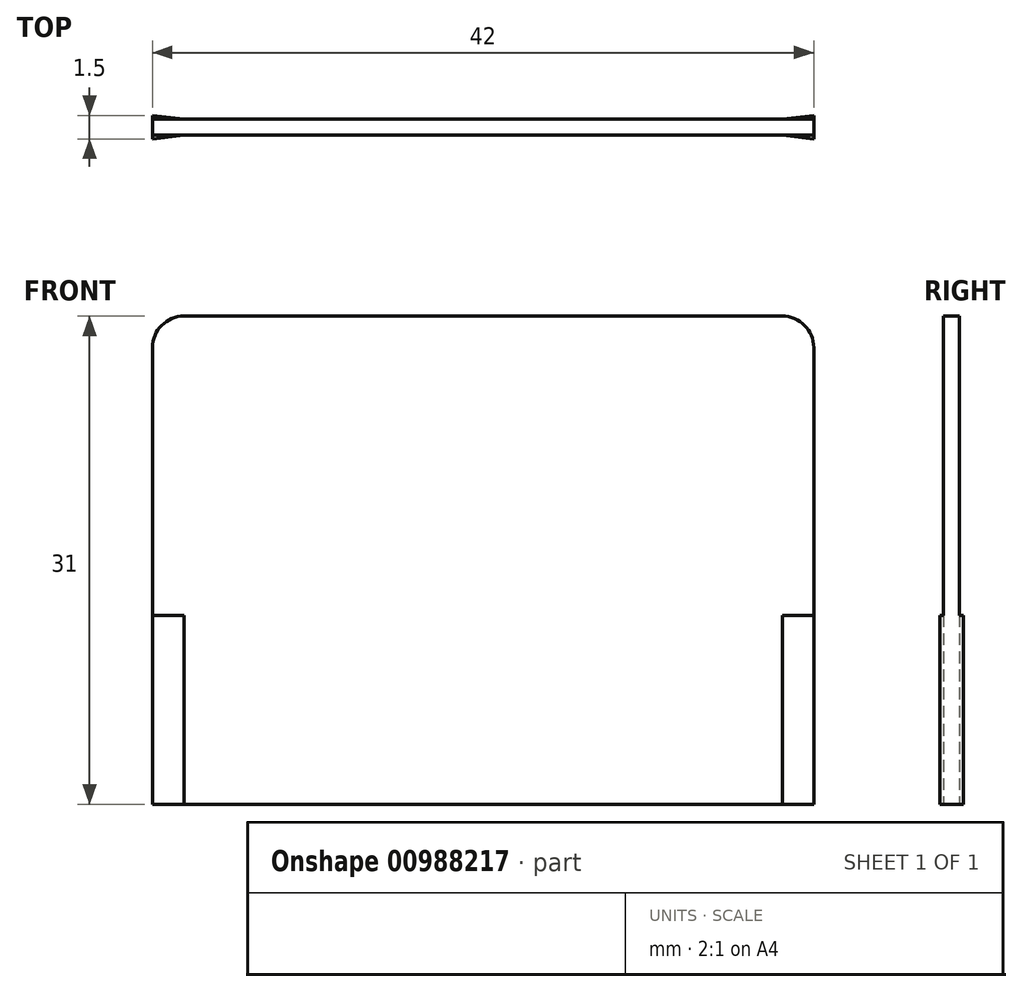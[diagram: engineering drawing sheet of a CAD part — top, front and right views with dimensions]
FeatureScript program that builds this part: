
annotation { "Feature Type Name" : "Feature", "Feature Type Description" : "" }
export const myFeature = defineFeature(function(context is Context, id is Id, definition is map)
    precondition{}
    {
        {
            assignVariable(context, id + "F0", {"variableType" : VariableType.LENGTH, "name" : "Height", "lengthValue" : 31 * mm});
        }
        {
            var Q0;
            Q0=qCreatedBy(makeId("Top.planeOp"),FACE);
            var sketch = newSketch(context, id + "F1", { "sketchPlane" : qUnion([Q0])});
            skLineSegment(sketch, "E0.bottom", {"start": v(-21, 0.5) * mm, "end": v(21, 0.5) * mm});
            skLineSegment(sketch, "E0.top", {"start": v(-21, -0.5) * mm, "end": v(21, -0.5) * mm});
            skLineSegment(sketch, "E0.left", {"start": v(-21, 0.5) * mm, "end": v(-21, -0.5) * mm});
            skLineSegment(sketch, "E0.right", {"start": v(21, 0.5) * mm, "end": v(21, -0.5) * mm});
            skLineSegment(sketch, "E1", {"start": v(-21, 0.75) * mm, "end": v(-21, -0.75) * mm});
            skLineSegment(sketch, "E2", {"start": v(-21, -0.75) * mm, "end": v(-19, -0.5) * mm});
            skLineSegment(sketch, "E3", {"start": v(-19, -0.5) * mm, "end": v(-21, -0.5) * mm});
            skLineSegment(sketch, "E4", {"start": v(-21, 0.75) * mm, "end": v(-19, 0.5) * mm});
            skLineSegment(sketch, "E5", {"start": v(-19, 0.5) * mm, "end": v(-21, 0.5) * mm});
            skLineSegment(sketch, "E6.MirrorCS", {"start": v(21, 0.75) * mm, "end": v(19, 0.5) * mm});
            skLineSegment(sketch, "E7.MirrorCS", {"start": v(21, 0.75) * mm, "end": v(21, -0.75) * mm});
            skLineSegment(sketch, "E8.MirrorCS", {"start": v(21, -0.75) * mm, "end": v(19, -0.5) * mm});
            skLineSegment(sketch, "E9.MirrorCS", {"start": v(21, -0.5) * mm, "end": v(-21, -0.5) * mm});
            skSolve(sketch);
        }
        {
            var Q0;
            Q0=makeQuery(id+"F1.imprint","IMPRINT",FACE,{"disambiguationData":[TD([[makeQuery(id+"F1.imprint","IMPRINT",EDGE,{"derivedFrom":sQuery(id+"F1.wireOp",EDGE,"E0.bottom")}),-1.0]])]});
            extrude(context, id + "F2", {"entities" : qUnion([Q0]), "depth" : getVariable(context, 'Height'), "offsetDistance" : 25 * mm});
        }
        {
            var Q0;
            {var subQ0=sQuery(id+"F1.wireOp",EDGE,"E4");Q0=makeQuery(id+"F1.imprint","IMPRINT",FACE,{"disambiguationData":[TD([[makeQuery(id+"F1.imprint","IMPRINT",EDGE,{"derivedFrom":subQ0}),-1.0]])]});}
            var Q1;
            {var subQ0=sQuery(id+"F1.wireOp",EDGE,"E2");Q1=makeQuery(id+"F1.imprint","IMPRINT",FACE,{"disambiguationData":[TD([[makeQuery(id+"F1.imprint","IMPRINT",EDGE,{"derivedFrom":subQ0}),1.0]])]});}
            var Q2;
            {var subQ3=sQuery(id+"F1.wireOp",EDGE,"E6.MirrorCS");Q2=makeQuery(id+"F1.imprint","IMPRINT",FACE,{"disambiguationData":[TD([[makeQuery(id+"F1.imprint","IMPRINT",EDGE,{"derivedFrom":subQ3}),1.0]])]});}
            var Q3;
            {var subQ3=sQuery(id+"F1.wireOp",EDGE,"E8.MirrorCS");Q3=makeQuery(id+"F1.imprint","IMPRINT",FACE,{"disambiguationData":[TD([[makeQuery(id+"F1.imprint","IMPRINT",EDGE,{"derivedFrom":subQ3}),-1.0]])]});}
            extrude(context, id + "F3", {"entities" : qUnion([Q0, Q1, Q2, Q3]), "operationType" : NewBodyOperationType.ADD, "depth" : 12 * mm, "offsetDistance" : 25 * mm});
        }
        {
            var Q0;
            Q0=makeQuery(id+"F2.opExtrude","CAP_EDGE",EDGE,{"disambiguationData":[OSD([sQuery(id+"F1.wireOp",EDGE,"E0.left")])],"isStart":false});
            var Q1;
            Q1=makeQuery(id+"F2.opExtrude","CAP_EDGE",EDGE,{"disambiguationData":[OSD([sQuery(id+"F1.wireOp",EDGE,"E0.right")])],"isStart":false});
            fillet(context, id + "F4", {"entities" : qUnion([Q0, Q1]), "tangentPropagation" : true, "radius" : 2 * mm, "defaultsChanged" : true, "vertexSettings" : [], "allowEdgeOverflow" : false});
        }
    });
